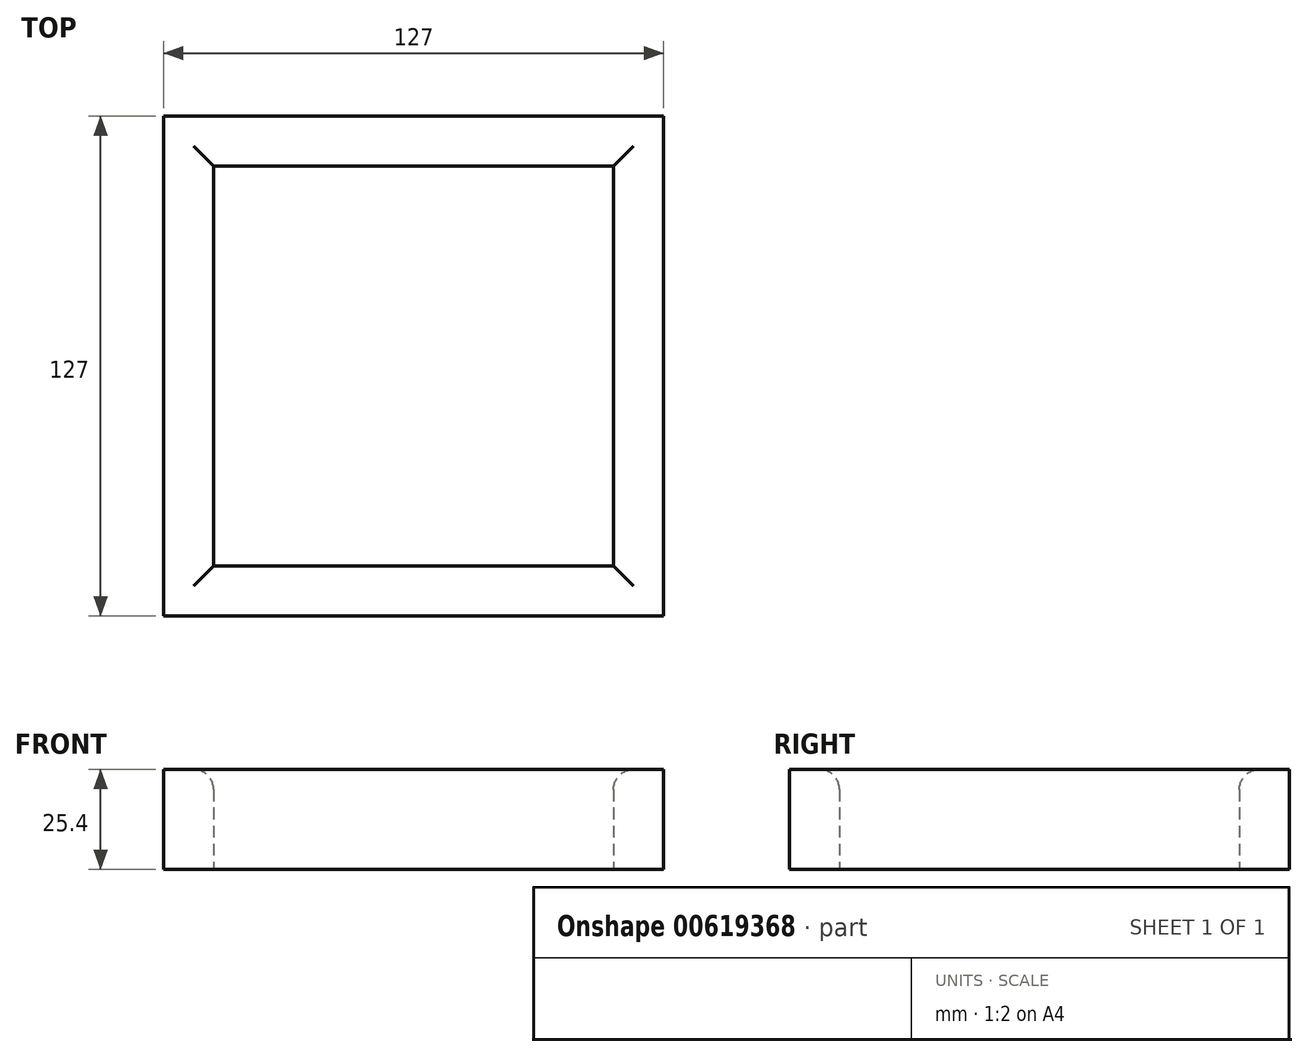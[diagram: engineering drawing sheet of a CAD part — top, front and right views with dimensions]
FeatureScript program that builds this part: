
annotation { "Feature Type Name" : "Feature", "Feature Type Description" : "" }
export const myFeature = defineFeature(function(context is Context, id is Id, definition is map)
    precondition{}
    {
        {
            var Q0;
            Q0=qCreatedBy(makeId("Top.planeOp"),FACE);
            var sketch = newSketch(context, id + "F0", { "sketchPlane" : qUnion([Q0])});
            skLineSegment(sketch, "E0.bottom", {"start": v(-54.53, 57.43) * mm, "end": v(72.47, 57.43) * mm});
            skLineSegment(sketch, "E0.top", {"start": v(-54.53, -69.57) * mm, "end": v(72.47, -69.57) * mm});
            skLineSegment(sketch, "E0.left", {"start": v(-54.53, 57.43) * mm, "end": v(-54.53, -69.57) * mm});
            skLineSegment(sketch, "E0.right", {"start": v(72.47, 57.43) * mm, "end": v(72.47, -69.57) * mm});
            skSolve(sketch);
        }
        {
            var Q0;
            Q0=makeQuery(id+"F0.imprint","IMPRINT",FACE,{"disambiguationData":[TD([[makeQuery(id+"F0.imprint","IMPRINT",EDGE,{"derivedFrom":sQuery(id+"F0.wireOp",EDGE,"E0.bottom")}),-1.0]])]});
            var sketch = newSketch(context, id + "F1", { "sketchPlane" : qUnion([Q0])});
            skLineSegment(sketch, "E1.bottom", {"start": v(-41.83, 44.73) * mm, "end": v(59.77, 44.73) * mm});
            skLineSegment(sketch, "E1.top", {"start": v(-41.83, -56.87) * mm, "end": v(59.77, -56.87) * mm});
            skLineSegment(sketch, "E1.left", {"start": v(-41.83, 44.73) * mm, "end": v(-41.83, -56.87) * mm});
            skLineSegment(sketch, "E1.right", {"start": v(59.77, 44.73) * mm, "end": v(59.77, -56.87) * mm});
            skSolve(sketch);
        }
        {
            var Q0;
            Q0=makeQuery(id+"F1.imprint","IMPRINT",FACE,{"disambiguationData":[TD([[makeQuery(id+"F1.imprint","IMPRINT",EDGE,{"derivedFrom":sQuery(id+"F1.wireOp",EDGE,"E1.bottom")}),1.0]])]});
            extrude(context, id + "F2", {"entities" : qUnion([Q0]), "depth" : 25.4 * mm, "offsetDistance" : 25.4 * mm});
        }
        {
            var Q0;
            Q0=makeQuery(id+"F2.opExtrude","CAP_EDGE",EDGE,{"disambiguationData":[OSD([sQuery(id+"F1.wireOp",EDGE,"E1.top")])],"isStart":false});
            var Q1;
            Q1=makeQuery(id+"F2.opExtrude","CAP_EDGE",EDGE,{"disambiguationData":[OSD([sQuery(id+"F1.wireOp",EDGE,"E1.right")])],"isStart":false});
            var Q2;
            Q2=makeQuery(id+"F2.opExtrude","CAP_EDGE",EDGE,{"disambiguationData":[OSD([sQuery(id+"F1.wireOp",EDGE,"E1.left")])],"isStart":false});
            var Q3;
            Q3=makeQuery(id+"F2.opExtrude","CAP_EDGE",EDGE,{"disambiguationData":[OSD([sQuery(id+"F1.wireOp",EDGE,"E1.bottom")])],"isStart":false});
            fillet(context, id + "F3", {"entities" : qUnion([Q0, Q1, Q2, Q3]), "radius" : 5.08 * mm, "tangentPropagation" : true, "allowEdgeOverflow" : false});
        }
    });
